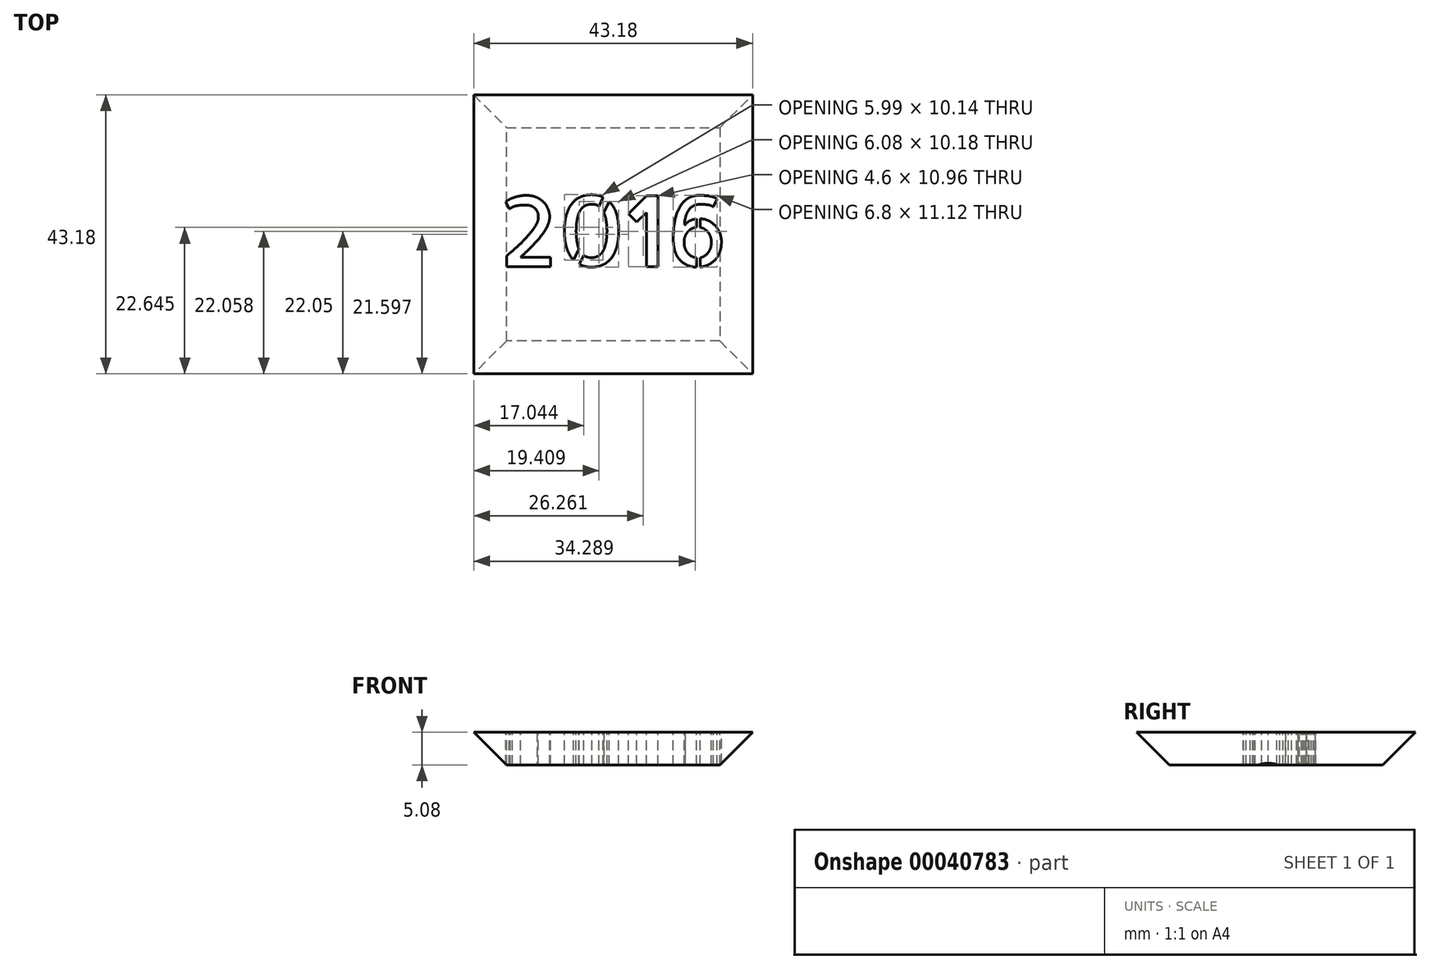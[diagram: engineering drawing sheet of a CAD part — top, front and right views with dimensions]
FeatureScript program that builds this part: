
annotation { "Feature Type Name" : "Feature", "Feature Type Description" : "" }
export const myFeature = defineFeature(function(context is Context, id is Id, definition is map)
    precondition{}
    {
        {
            var Q0;
            Q0=qCreatedBy(makeId("Top.planeOp"),FACE);
            var sketch = newSketch(context, id + "F0", { "sketchPlane" : qUnion([Q0])});
            skLineSegment(sketch, "E0.bottom", {"start": v(-34.02, 13.72) * mm, "end": v(9.16, 13.72) * mm});
            skLineSegment(sketch, "E0.top", {"start": v(-34.02, -29.46) * mm, "end": v(9.16, -29.46) * mm});
            skLineSegment(sketch, "E0.left", {"start": v(-34.02, 13.72) * mm, "end": v(-34.02, -29.46) * mm});
            skLineSegment(sketch, "E0.right", {"start": v(9.16, 13.72) * mm, "end": v(9.16, -29.46) * mm});
            skText(sketch, "E1", { "text": "2016\n", "fontName": "AllertaStencil-Regular.ttf"});
            const initialGuessF0  = {"E1": [-0.0302, -0.01288, 1, 0, 0.01096]};
            skSetInitialGuess(sketch, initialGuessF0);
            skSolve(sketch);
        }
        {
            var Q0;
            Q0=makeQuery(id+"F0.imprint","IMPRINT",FACE,{"disambiguationData":[TD([[makeQuery(id+"F0.imprint","IMPRINT",EDGE,{"derivedFrom":sQuery(id+"F0.wireOp",EDGE,"E0.bottom")}),-1.0]])]});
            extrude(context, id + "F1", {"entities" : qUnion([Q0]), "oppositeDirection" : true, "depth" : 5.08 * mm});
        }
        {
            var Q0;
            Q0=makeQuery(id+"F1.opExtrude","CAP_EDGE",EDGE,{"disambiguationData":[OSD([sQuery(id+"F0.wireOp",EDGE,"E0.right")])],"isStart":false});
            var Q1;
            Q1=makeQuery(id+"F1.opExtrude","CAP_EDGE",EDGE,{"disambiguationData":[OSD([sQuery(id+"F0.wireOp",EDGE,"E0.bottom")])],"isStart":false});
            var Q2;
            Q2=makeQuery(id+"F1.opExtrude","CAP_EDGE",EDGE,{"disambiguationData":[OSD([sQuery(id+"F0.wireOp",EDGE,"E0.left")])],"isStart":false});
            var Q3;
            Q3=makeQuery(id+"F1.opExtrude","CAP_EDGE",EDGE,{"disambiguationData":[OSD([sQuery(id+"F0.wireOp",EDGE,"E0.top")])],"isStart":false});
            chamfer(context, id + "F2", {"entities" : qUnion([Q0, Q1, Q2, Q3]), "width" : 5.08 * mm, "tangentPropagation" : true});
        }
    });
